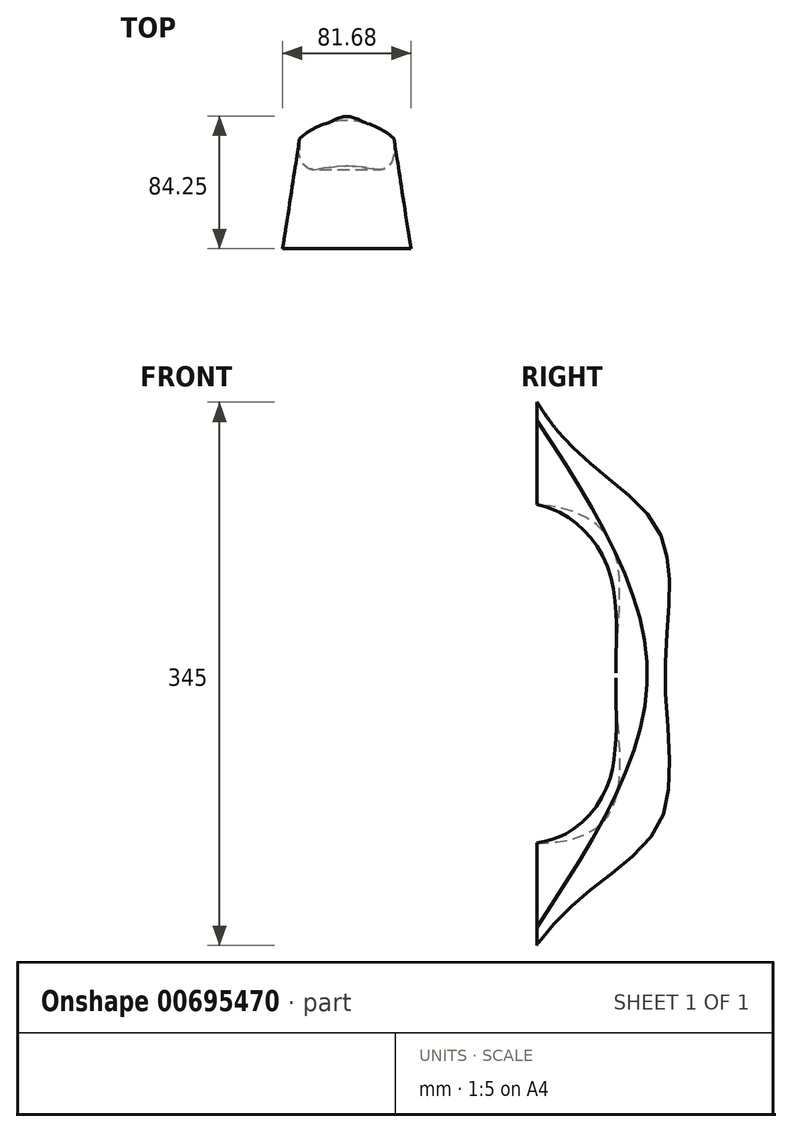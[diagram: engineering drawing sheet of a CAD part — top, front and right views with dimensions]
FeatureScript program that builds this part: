
annotation { "Feature Type Name" : "Feature", "Feature Type Description" : "" }
export const myFeature = defineFeature(function(context is Context, id is Id, definition is map)
    precondition{}
    {
        {
            var Q0;
            Q0=qCreatedBy(makeId("Front.planeOp"),FACE);
            var sketch = newSketch(context, id + "F0", { "sketchPlane" : qUnion([Q0])});
            skLineSegment(sketch, "E0", {"start": v(-30.84, 175) * mm, "end": v(30.84, 175) * mm});
            skLineSegment(sketch, "E1", {"start": v(-23.92, 110) * mm, "end": v(23.92, 110) * mm});
            skLineSegment(sketch, "E2", {"start": v(40.73, 163.48) * mm, "end": v(33.8, 118.48) * mm});
            skLineSegment(sketch, "E3", {"start": v(-33.8, 118.48) * mm, "end": v(-40.73, 163.48) * mm});
            skPoint(sketch, "E4.visualSharp", {"position": v(-42.5, 175) * mm});
            skArc(sketch, "E4.filletArc", {"start": v(-30.84, 175) * mm, "mid": v(-38.43, 171.51) * mm, "end": v(-40.73, 163.48) * mm});
            skPoint(sketch, "E5.visualSharp", {"position": v(42.5, 175) * mm});
            skArc(sketch, "E5.filletArc", {"start": v(40.73, 163.48) * mm, "mid": v(38.43, 171.51) * mm, "end": v(30.84, 175) * mm});
            skPoint(sketch, "E6.visualSharp", {"position": v(32.5, 110) * mm});
            skArc(sketch, "E6.filletArc", {"start": v(23.92, 110) * mm, "mid": v(30.43, 112.41) * mm, "end": v(33.8, 118.48) * mm});
            skPoint(sketch, "E7.visualSharp", {"position": v(-32.5, 110) * mm});
            skArc(sketch, "E7.filletArc", {"start": v(-33.8, 118.48) * mm, "mid": v(-30.43, 112.41) * mm, "end": v(-23.92, 110) * mm});
            skLineSegment(sketch, "E8", {"start": v(0, 103.27) * mm, "end": v(0, 189.26) * mm, "construction": true});
            skSolve(sketch);
        }
        {
            var Q0;
            Q0=qCreatedBy(makeId("Top.planeOp"),FACE);
            var sketch = newSketch(context, id + "F1", { "sketchPlane" : qUnion([Q0])});
            skLineSegment(sketch, "E9", {"start": v(-20, 50) * mm, "end": v(20, 50) * mm});
            skLineSegment(sketch, "E10", {"start": v(-30, 60) * mm, "end": v(-30, 70) * mm});
            skLineSegment(sketch, "E11", {"start": v(30, 60) * mm, "end": v(30, 70) * mm});
            skArc(sketch, "E12", {"start": v(30, 70) * mm, "mid": v(0, 81.46) * mm, "end": v(-30, 70) * mm});
            skPoint(sketch, "E13.visualSharp", {"position": v(-30, 50) * mm});
            skArc(sketch, "E13.filletArc", {"start": v(-30, 60) * mm, "mid": v(-27.07, 52.93) * mm, "end": v(-20, 50) * mm});
            skPoint(sketch, "E14.visualSharp", {"position": v(30, 50) * mm});
            skArc(sketch, "E14.filletArc", {"start": v(20, 50) * mm, "mid": v(27.07, 52.93) * mm, "end": v(30, 60) * mm});
            skSolve(sketch);
        }
        {
            var Q0;
            Q0=qCreatedBy(makeId("Front.planeOp"),FACE);
            var sketch = newSketch(context, id + "F2", { "sketchPlane" : qUnion([Q0])});
            skLineSegment(sketch, "E15", {"start": v(30.84, -170) * mm, "end": v(-30.84, -170) * mm});
            skLineSegment(sketch, "E16", {"start": v(23.92, -105) * mm, "end": v(-23.92, -105) * mm});
            skLineSegment(sketch, "E17", {"start": v(-40.73, -158.48) * mm, "end": v(-33.8, -113.48) * mm});
            skLineSegment(sketch, "E18", {"start": v(33.8, -113.48) * mm, "end": v(40.73, -158.48) * mm});
            skPoint(sketch, "E19.visualSharp", {"position": v(42.5, -170) * mm});
            skArc(sketch, "E19.filletArc", {"start": v(30.84, -170) * mm, "mid": v(38.43, -166.51) * mm, "end": v(40.73, -158.48) * mm});
            skPoint(sketch, "E20.visualSharp", {"position": v(-42.5, -170) * mm});
            skArc(sketch, "E20.filletArc", {"start": v(-40.73, -158.48) * mm, "mid": v(-38.43, -166.51) * mm, "end": v(-30.84, -170) * mm});
            skPoint(sketch, "E21.visualSharp", {"position": v(-32.5, -105) * mm});
            skArc(sketch, "E21.filletArc", {"start": v(-23.92, -105) * mm, "mid": v(-30.43, -107.41) * mm, "end": v(-33.8, -113.48) * mm});
            skPoint(sketch, "E22.visualSharp", {"position": v(32.5, -105) * mm});
            skArc(sketch, "E22.filletArc", {"start": v(33.8, -113.48) * mm, "mid": v(30.43, -107.41) * mm, "end": v(23.92, -105) * mm});
            skSolve(sketch);
        }
        {
            var Q0;
            Q0=qCreatedBy(makeId("Right.planeOp"),FACE);
            var sketch = newSketch(context, id + "F3", { "sketchPlane" : qUnion([Q0])});
            skPoint(sketch, "E23.0", {"position": v(0, 175) * mm});
            skPoint(sketch, "E24.0", {"position": v(81.46, 0) * mm});
            skPoint(sketch, "E25.0", {"position": v(0, -170) * mm});
            skPoint(sketch, "E26", {"position": v(77.04, -93.94) * mm});
            skPoint(sketch, "E27", {"position": v(77.04, 93.94) * mm});
            skFitSpline(sketch, "E28", {"points": [v(0, 175) * mm, v(77.04, 93.94) * mm, v(81.46, 0) * mm, v(77.04, -93.94) * mm, v(0, -170) * mm], "startDerivative": vector(281.37, -473.5) * mm, "endDerivative": vector(-285.97, -423.05) * mm});
            skPoint(sketch, "E29.0", {"position": v(0, -105) * mm});
            skPoint(sketch, "E29.1", {"position": v(0, 110) * mm});
            skPoint(sketch, "E30.0", {"position": v(50, 0) * mm});
            skFitSpline(sketch, "E31", {"points": [v(0, -105) * mm, v(50, 0) * mm, v(0, 110) * mm], "startDerivative": vector(422.86, 3.36) * mm, "endDerivative": vector(-414.85, 33.01) * mm});
            skSolve(sketch);
        }
        {
            var Q0;
            Q0=makeQuery(id+"F0.imprint","IMPRINT",FACE,{"disambiguationData":[TD([[makeQuery(id+"F0.imprint","IMPRINT",EDGE,{"derivedFrom":sQuery(id+"F0.wireOp",EDGE,"E0")}),-1.0]])]});
            var Q1;
            Q1=makeQuery(id+"F1.imprint","IMPRINT",FACE,{"disambiguationData":[TD([[makeQuery(id+"F1.imprint","IMPRINT",EDGE,{"derivedFrom":sQuery(id+"F1.wireOp",EDGE,"E9")}),1.0]])]});
            var Q2;
            Q2=makeQuery(id+"F2.imprint","IMPRINT",FACE,{"disambiguationData":[TD([[makeQuery(id+"F2.imprint","IMPRINT",EDGE,{"derivedFrom":sQuery(id+"F2.wireOp",EDGE,"E15")}),-1.0]])]});
            var Q3;
            Q3=sQuery(id+"F3.wireOp",EDGE,"E28");
            var Q4;
            Q4=sQuery(id+"F3.wireOp",EDGE,"E31");
            var Q5;
            Q5=sQuery(id+"F3.wireOp",EDGE,"E28");
            var Q6;
            Q6=sQuery(id+"F3.wireOp",VERTEX,"E23.0");
            var Q7;
            Q7=sQuery(id+"F3.wireOp",VERTEX,"E24.0");
            var Q8;
            Q8=sQuery(id+"F3.wireOp",VERTEX,"E25.0");
            loft(context, id + "F4", {"sheetProfilesArray" : [{ "sheetProfileEntities" : qUnion([Q0]) }, { "sheetProfileEntities" : qUnion([Q1]) }, { "sheetProfileEntities" : qUnion([Q2]) }], "addGuides" : true, "guidesArray" : [{ "guideEntities" : qUnion([Q3]), "guideDerivativeType" : LoftGuideDerivativeType.DEFAULT, "guideDerivativeMagnitude" : 1 }, { "guideEntities" : qUnion([Q4]), "guideDerivativeType" : LoftGuideDerivativeType.DEFAULT, "guideDerivativeMagnitude" : 1 }], "spine" : qUnion([Q5]), "connections" : [{ "connectionEntities" : qUnion([Q6, Q7, Q8]), "connectionEdgeQueries" : qUnion([]), "connectionEdgeParameters" : [] }]});
        }
    });
